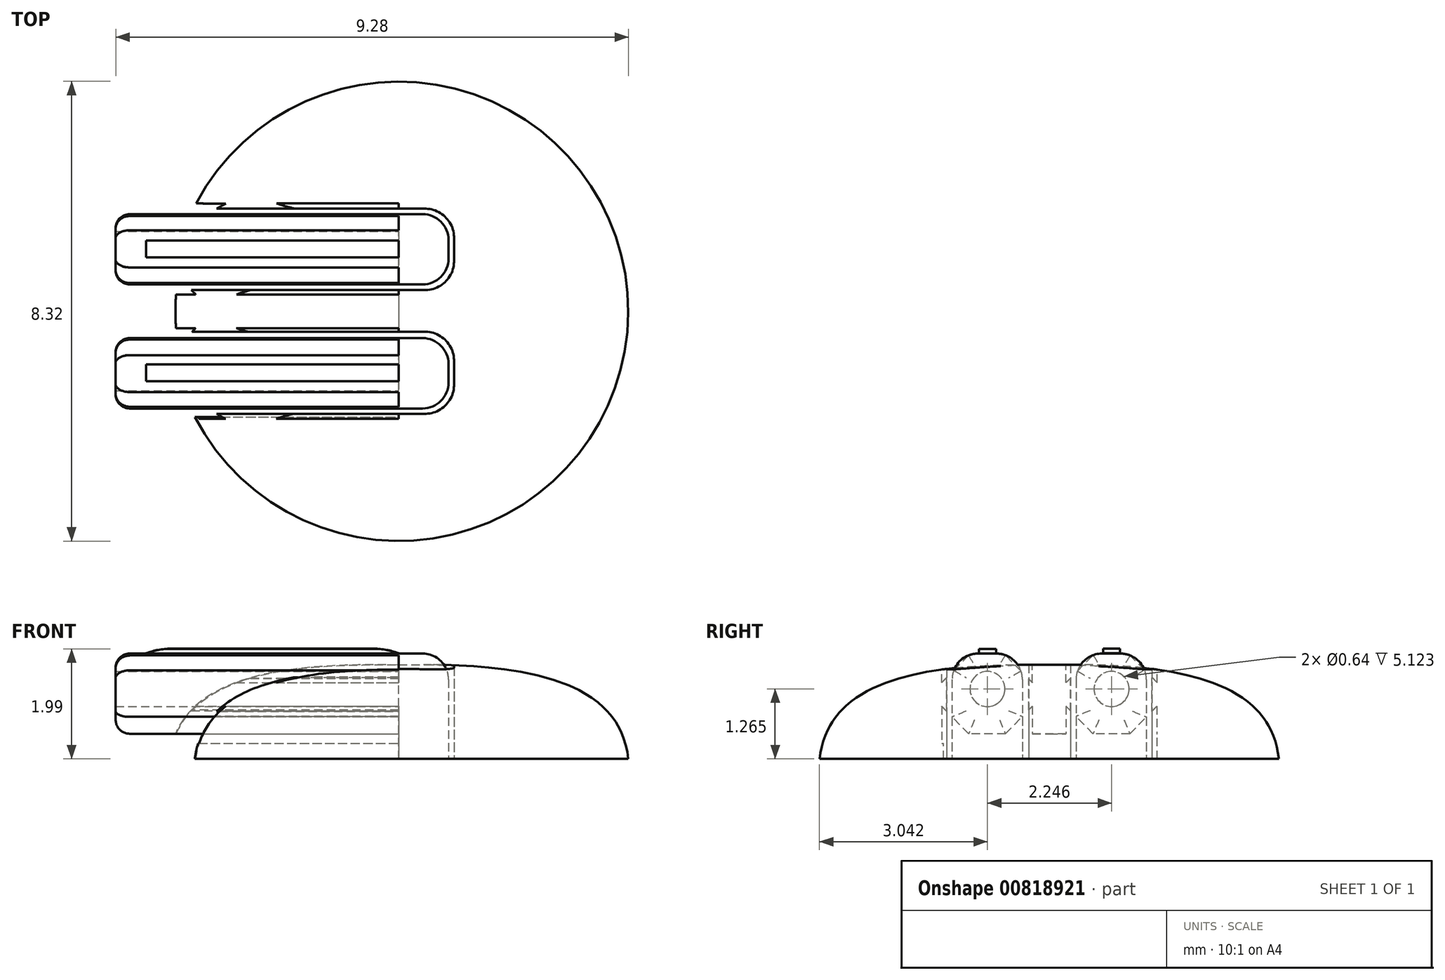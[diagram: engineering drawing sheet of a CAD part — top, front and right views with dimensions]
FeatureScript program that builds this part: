
annotation { "Feature Type Name" : "Feature", "Feature Type Description" : "" }
export const myFeature = defineFeature(function(context is Context, id is Id, definition is map)
    precondition{}
    {
        {
            var Q0;
            Q0=qCreatedBy(makeId("Front.planeOp"),FACE);
            var sketch = newSketch(context, id + "F0", { "sketchPlane" : qUnion([Q0])});
            skFitSpline(sketch, "E0", {"points": [v(0, 1.7) * mm, v(-4.16, 0) * mm], "startDerivative": vector(-6.44, 0.15) * mm, "endDerivative": vector(-0.46, -4.44) * mm});
            skLineSegment(sketch, "E1", {"start": v(-4.16, 0) * mm, "end": v(0, 0) * mm});
            skLineSegment(sketch, "E2", {"start": v(0, 0) * mm, "end": v(0, 1.7) * mm});
            skSolve(sketch);
        }
        {
            var Q0;
            Q0 = qSketchRegion(id + "F0", true);
            var Q1;
            Q1=sQuery(id+"F0.wireOp",EDGE,"E2");
            revolve(context, id + "F1", {"surfaceOperationType" : NewSurfaceOperationType.NEW, "entities" : qUnion([Q0]), "axis" : qUnion([Q1]), "revolveType" : RevolveType.FULL});
        }
        {
            var Q0;
            Q0=qCreatedBy(makeId("Top.planeOp"),FACE);
            var sketch = newSketch(context, id + "F2", { "sketchPlane" : qUnion([Q0])});
            skLineSegment(sketch, "E3.bottom", {"start": v(-4.22, 0.38) * mm, "end": v(1, 0.38) * mm});
            skLineSegment(sketch, "E3.top", {"start": v(-4.22, 1.86) * mm, "end": v(1, 1.86) * mm});
            skLineSegment(sketch, "E3.left", {"start": v(-4.22, 0.38) * mm, "end": v(-4.22, 1.86) * mm});
            skLineSegment(sketch, "E3.right", {"start": v(1, 0.38) * mm, "end": v(1, 1.86) * mm});
            skLineSegment(sketch, "E4.bottom", {"start": v(-4.22, -1.85) * mm, "end": v(1, -1.85) * mm});
            skLineSegment(sketch, "E4.top", {"start": v(-4.22, -0.37) * mm, "end": v(1, -0.37) * mm});
            skLineSegment(sketch, "E4.left", {"start": v(-4.22, -1.85) * mm, "end": v(-4.22, -0.37) * mm});
            skLineSegment(sketch, "E4.right", {"start": v(1, -1.85) * mm, "end": v(1, -0.37) * mm});
            skSolve(sketch);
        }
        {
            var Q0;
            Q0 = qSketchRegion(id + "F2", true);
            extrude(context, id + "F3", {"entities" : qUnion([Q0]), "operationType" : NewBodyOperationType.REMOVE, "depth" : 1.78 * mm, "offsetDistance" : 25.4 * mm});
        }
        {
            var Q0;
            Q0=qCreatedBy(makeId("Top.planeOp"),FACE);
            var sketch = newSketch(context, id + "F4", { "sketchPlane" : qUnion([Q0])});
            skLineSegment(sketch, "E5.bottom", {"start": v(-5.12, -1.76) * mm, "end": v(0.9, -1.76) * mm});
            skLineSegment(sketch, "E5.top", {"start": v(-5.12, -0.49) * mm, "end": v(0.9, -0.49) * mm});
            skLineSegment(sketch, "E5.left", {"start": v(-5.12, -1.76) * mm, "end": v(-5.12, -0.49) * mm});
            skLineSegment(sketch, "E5.right", {"start": v(0.9, -1.76) * mm, "end": v(0.9, -0.49) * mm});
            skLineSegment(sketch, "E6.bottom", {"start": v(-5.12, 0.48) * mm, "end": v(0.9, 0.48) * mm});
            skLineSegment(sketch, "E6.top", {"start": v(-5.12, 1.76) * mm, "end": v(0.9, 1.76) * mm});
            skLineSegment(sketch, "E6.left", {"start": v(-5.12, 0.48) * mm, "end": v(-5.12, 1.76) * mm});
            skLineSegment(sketch, "E6.right", {"start": v(0.9, 0.48) * mm, "end": v(0.9, 1.76) * mm});
            skSolve(sketch);
        }
        {
            var Q0;
            Q0 = qSketchRegion(id + "F4", true);
            extrude(context, id + "F5", {"entities" : qUnion([Q0]), "depth" : 1.9 * mm, "offsetDistance" : 25.4 * mm});
        }
        {
            var Q0;
            Q0=qCreatedBy(makeId("Right.planeOp"),FACE);
            var sketch = newSketch(context, id + "F6", { "sketchPlane" : qUnion([Q0])});
            skLineSegment(sketch, "E7.bottom", {"start": v(1.95, 0) * mm, "end": v(-1.91, 0) * mm});
            skLineSegment(sketch, "E7.top", {"start": v(1.95, 0.45) * mm, "end": v(-1.91, 0.45) * mm});
            skLineSegment(sketch, "E7.left", {"start": v(1.95, 0) * mm, "end": v(1.95, 0.45) * mm});
            skLineSegment(sketch, "E7.right", {"start": v(-1.91, 0) * mm, "end": v(-1.91, 0.45) * mm});
            skLineSegment(sketch, "E8", {"start": v(1.95, 2.05) * mm, "end": v(1.28, 2.05) * mm});
            skLineSegment(sketch, "E9", {"start": v(1.28, 2.05) * mm, "end": v(1.95, 1.38) * mm});
            skLineSegment(sketch, "E10", {"start": v(1.95, 1.38) * mm, "end": v(1.95, 2.05) * mm});
            skLineSegment(sketch, "E11", {"start": v(-0.3, 2.05) * mm, "end": v(-0.97, 2.05) * mm});
            skLineSegment(sketch, "E12", {"start": v(-0.97, 2.05) * mm, "end": v(-0.3, 1.38) * mm});
            skLineSegment(sketch, "E13", {"start": v(-0.3, 1.38) * mm, "end": v(-0.3, 2.05) * mm});
            skLineSegment(sketch, "E14.MirrorCS", {"start": v(-1.95, 2.05) * mm, "end": v(-1.28, 2.05) * mm});
            skLineSegment(sketch, "E15.MirrorCS", {"start": v(-1.95, 1.38) * mm, "end": v(-1.95, 2.05) * mm});
            skLineSegment(sketch, "E16.MirrorCS", {"start": v(0.3, 2.05) * mm, "end": v(0.97, 2.05) * mm});
            skLineSegment(sketch, "E17.MirrorCS", {"start": v(0.97, 2.05) * mm, "end": v(0.3, 1.38) * mm});
            skLineSegment(sketch, "E18.MirrorCS", {"start": v(-1.28, 2.05) * mm, "end": v(-1.95, 1.38) * mm});
            skLineSegment(sketch, "E19.MirrorCS", {"start": v(0.3, 1.38) * mm, "end": v(0.3, 2.05) * mm});
            skLineSegment(sketch, "E20.MirrorCS", {"start": v(0.97, 0.28) * mm, "end": v(0.3, 0.95) * mm});
            skLineSegment(sketch, "E21.MirrorCS", {"start": v(-1.28, 0.28) * mm, "end": v(-1.95, 0.95) * mm});
            skLineSegment(sketch, "E22.MirrorCS", {"start": v(0.3, 0.95) * mm, "end": v(0.3, 0.28) * mm});
            skLineSegment(sketch, "E23.MirrorCS", {"start": v(1.95, 0.95) * mm, "end": v(1.95, 0.28) * mm});
            skLineSegment(sketch, "E24.MirrorCS", {"start": v(0.3, 0.28) * mm, "end": v(0.97, 0.28) * mm});
            skLineSegment(sketch, "E25.MirrorCS", {"start": v(-0.3, 0.28) * mm, "end": v(-0.97, 0.28) * mm});
            skLineSegment(sketch, "E26.MirrorCS", {"start": v(1.28, 0.28) * mm, "end": v(1.95, 0.95) * mm});
            skLineSegment(sketch, "E27.MirrorCS", {"start": v(-0.97, 0.28) * mm, "end": v(-0.3, 0.95) * mm});
            skLineSegment(sketch, "E28.MirrorCS", {"start": v(-0.3, 0.95) * mm, "end": v(-0.3, 0.28) * mm});
            skLineSegment(sketch, "E29.MirrorCS", {"start": v(-1.95, 0.28) * mm, "end": v(-1.28, 0.28) * mm});
            skLineSegment(sketch, "E30.MirrorCS", {"start": v(1.95, 0.28) * mm, "end": v(1.28, 0.28) * mm});
            skLineSegment(sketch, "E31.MirrorCS", {"start": v(-1.95, 0.95) * mm, "end": v(-1.95, 0.28) * mm});
            skSolve(sketch);
        }
        {
            var Q0;
            Q0 = qSketchRegion(id + "F6", true);
            extrude(context, id + "F7", {"entities" : qUnion([Q0]), "operationType" : NewBodyOperationType.REMOVE, "oppositeDirection" : true, "depth" : 5.7 * mm, "offsetDistance" : 25.4 * mm});
        }
        {
            var Q0;
            Q0=makeQuery(id+"F5.opExtrude","CAP_EDGE",EDGE,{"disambiguationData":[OSD([sQuery(id+"F4.wireOp",EDGE,"E6.right")])],"isStart":false});
            var Q1;
            Q1=makeQuery(id+"F5.opExtrude","CAP_EDGE",EDGE,{"disambiguationData":[OSD([sQuery(id+"F4.wireOp",EDGE,"E6.bottom")])],"isStart":false});
            var Q2;
            Q2=makeQuery(id+"F5.opExtrude","CAP_EDGE",EDGE,{"disambiguationData":[OSD([sQuery(id+"F4.wireOp",EDGE,"E6.top")])],"isStart":false});
            var Q3;
            Q3=makeQuery(id+"F5.opExtrude","CAP_EDGE",EDGE,{"disambiguationData":[OSD([sQuery(id+"F4.wireOp",EDGE,"E5.bottom")])],"isStart":false});
            var Q4;
            Q4=makeQuery(id+"F5.opExtrude","CAP_EDGE",EDGE,{"disambiguationData":[OSD([sQuery(id+"F4.wireOp",EDGE,"E5.right")])],"isStart":false});
            var Q5;
            Q5=makeQuery(id+"F5.opExtrude","CAP_EDGE",EDGE,{"disambiguationData":[OSD([sQuery(id+"F4.wireOp",EDGE,"E5.top")])],"isStart":false});
            var Q6;
            Q6=makeQuery(id+"F5.opExtrude","SWEPT_EDGE",EDGE,{"disambiguationData":[OSD([sQuery(id+"F4.wireOp",EDGE,"E6.top"),sQuery(id+"F4.wireOp",EDGE,"E6.right")])]});
            var Q7;
            Q7=makeQuery(id+"F5.opExtrude","SWEPT_EDGE",EDGE,{"disambiguationData":[OSD([sQuery(id+"F4.wireOp",EDGE,"E6.bottom"),sQuery(id+"F4.wireOp",EDGE,"E6.right")])]});
            var Q8;
            Q8=makeQuery(id+"F5.opExtrude","SWEPT_EDGE",EDGE,{"disambiguationData":[OSD([sQuery(id+"F4.wireOp",EDGE,"E5.top"),sQuery(id+"F4.wireOp",EDGE,"E5.right")])]});
            var Q9;
            Q9=makeQuery(id+"F5.opExtrude","SWEPT_EDGE",EDGE,{"disambiguationData":[OSD([sQuery(id+"F4.wireOp",EDGE,"E5.bottom"),sQuery(id+"F4.wireOp",EDGE,"E5.right")])]});
            fillet(context, id + "F8", {"entities" : qUnion([Q0, Q1, Q2, Q3, Q4, Q5, Q6, Q7, Q8, Q9]), "radius" : 0.47 * mm, "tangentPropagation" : true, "allowEdgeOverflow" : false});
        }
        {
            var Q0;
            Q0=qCreatedBy(makeId("Right.planeOp"),FACE);
            var sketch = newSketch(context, id + "F9", { "sketchPlane" : qUnion([Q0])});
            skLineSegment(sketch, "E32.bottom", {"start": v(1.28, 2) * mm, "end": v(0.97, 2) * mm});
            skLineSegment(sketch, "E32.top", {"start": v(1.28, 1.91) * mm, "end": v(0.97, 1.91) * mm});
            skLineSegment(sketch, "E32.left", {"start": v(1.28, 2) * mm, "end": v(1.28, 1.91) * mm});
            skLineSegment(sketch, "E32.right", {"start": v(0.97, 2) * mm, "end": v(0.97, 1.91) * mm});
            skLineSegment(sketch, "E33.bottom", {"start": v(-0.96, 2) * mm, "end": v(-1.27, 2) * mm});
            skLineSegment(sketch, "E33.top", {"start": v(-0.96, 1.9) * mm, "end": v(-1.27, 1.9) * mm});
            skLineSegment(sketch, "E33.left", {"start": v(-0.96, 2) * mm, "end": v(-0.96, 1.9) * mm});
            skLineSegment(sketch, "E33.right", {"start": v(-1.27, 2) * mm, "end": v(-1.27, 1.9) * mm});
            skSolve(sketch);
        }
        {
            var Q0;
            Q0 = qSketchRegion(id + "F9", true);
            extrude(context, id + "F10", {"entities" : qUnion([Q0]), "oppositeDirection" : true, "depth" : 4.57 * mm, "offsetDistance" : 25.4 * mm});
        }
        {
            var Q0;
            Q0=qCreatedBy(makeId("Right.planeOp"),FACE);
            var sketch = newSketch(context, id + "F11", { "sketchPlane" : qUnion([Q0])});
            skCircle(sketch, "E34", {"center": v(1.13, 1.26) * mm, "radius": 0.32 * mm});
            skCircle(sketch, "E35", {"center": v(-1.12, 1.26) * mm, "radius": 0.32 * mm});
            skSolve(sketch);
        }
        {
            var Q0;
            Q0 = qSketchRegion(id + "F11", true);
            extrude(context, id + "F12", {"entities" : qUnion([Q0]), "operationType" : NewBodyOperationType.REMOVE, "oppositeDirection" : true, "depth" : 5.94 * mm, "offsetDistance" : 25.4 * mm});
        }
        {
            var Q0;
            Q0=makeQuery(id+"F3.boolean.opBoolean","COPY",EDGE,{"derivedFrom":makeQuery(id+"F3.opExtrude","SWEPT_EDGE",EDGE,{"disambiguationData":[OSD([sQuery(id+"F2.wireOp",EDGE,"E3.top"),sQuery(id+"F2.wireOp",EDGE,"E3.right")])]})});
            var Q1;
            Q1=makeQuery(id+"F3.boolean.opBoolean","COPY",EDGE,{"derivedFrom":makeQuery(id+"F3.opExtrude","SWEPT_EDGE",EDGE,{"disambiguationData":[OSD([sQuery(id+"F2.wireOp",EDGE,"E3.bottom"),sQuery(id+"F2.wireOp",EDGE,"E3.right")])]})});
            var Q2;
            Q2=makeQuery(id+"F3.boolean.opBoolean","COPY",EDGE,{"derivedFrom":makeQuery(id+"F3.opExtrude","SWEPT_EDGE",EDGE,{"disambiguationData":[OSD([sQuery(id+"F2.wireOp",EDGE,"E4.bottom"),sQuery(id+"F2.wireOp",EDGE,"E4.right")])]})});
            var Q3;
            Q3=makeQuery(id+"F3.boolean.opBoolean","COPY",EDGE,{"derivedFrom":makeQuery(id+"F3.opExtrude","SWEPT_EDGE",EDGE,{"disambiguationData":[OSD([sQuery(id+"F2.wireOp",EDGE,"E4.top"),sQuery(id+"F2.wireOp",EDGE,"E4.right")])]})});
            fillet(context, id + "F13", {"entities" : qUnion([Q0, Q1, Q2, Q3]), "radius" : 0.5 * mm, "tangentPropagation" : true, "allowEdgeOverflow" : false});
        }
        {
            var Q0;
            Q0=makeQuery(id+"F7.boolean.opBoolean","INTERSECT",EDGE,{"derivedFrom":[makeQuery(id+"F5.opExtrude","SWEPT_FACE",FACE,{"disambiguationData":[OSD([sQuery(id+"F4.wireOp",EDGE,"E6.left")])]}),makeQuery(id+"F7.opExtrude","SWEPT_FACE",FACE,{"disambiguationData":[OSD([sQuery(id+"F6.wireOp",EDGE,"E17.MirrorCS")])]})]});
            var Q1;
            Q1=makeQuery(id+"F5.opExtrude","SWEPT_EDGE",EDGE,{"disambiguationData":[OSD([sQuery(id+"F4.wireOp",EDGE,"E6.bottom"),sQuery(id+"F4.wireOp",EDGE,"E6.left")])]});
            var Q2;
            Q2=makeQuery(id+"F7.boolean.opBoolean","INTERSECT",EDGE,{"derivedFrom":[makeQuery(id+"F5.opExtrude","SWEPT_FACE",FACE,{"disambiguationData":[OSD([sQuery(id+"F4.wireOp",EDGE,"E6.left")])]}),makeQuery(id+"F7.opExtrude","SWEPT_FACE",FACE,{"disambiguationData":[OSD([sQuery(id+"F6.wireOp",EDGE,"E20.MirrorCS")])]})]});
            var Q3;
            {var subQ0=sQuery(id+"F6.wireOp",EDGE,"E7.top");Q3=makeQuery(id+"F7.boolean.opBoolean","INTERSECT",EDGE,{"derivedFrom":[makeQuery(id+"F5.opExtrude","SWEPT_FACE",FACE,{"disambiguationData":[OSD([sQuery(id+"F4.wireOp",EDGE,"E6.left")])]}),makeQuery(id+"F7.opExtrude","SWEPT_FACE",FACE,{"disambiguationData":[OSD([subQ0]),TDD([makeQuery(id+"F6.imprint","IMPRINT",EDGE,{"disambiguationData":[TD([[makeQuery(id+"F6.imprint","INTERSECT",VERTEX,{"derivedFrom":[subQ0,sQuery(id+"F6.wireOp",EDGE,"E26.MirrorCS")]}),-1.0]])],"derivedFrom":subQ0})])]})]});}
            var Q4;
            Q4=makeQuery(id+"F7.boolean.opBoolean","INTERSECT",EDGE,{"derivedFrom":[makeQuery(id+"F5.opExtrude","SWEPT_FACE",FACE,{"disambiguationData":[OSD([sQuery(id+"F4.wireOp",EDGE,"E6.left")])]}),makeQuery(id+"F7.opExtrude","SWEPT_FACE",FACE,{"disambiguationData":[OSD([sQuery(id+"F6.wireOp",EDGE,"E26.MirrorCS")])]})]});
            var Q5;
            Q5=makeQuery(id+"F5.opExtrude","SWEPT_EDGE",EDGE,{"disambiguationData":[OSD([sQuery(id+"F4.wireOp",EDGE,"E6.top"),sQuery(id+"F4.wireOp",EDGE,"E6.left")])]});
            var Q6;
            Q6=makeQuery(id+"F7.boolean.opBoolean","INTERSECT",EDGE,{"derivedFrom":[makeQuery(id+"F5.opExtrude","SWEPT_FACE",FACE,{"disambiguationData":[OSD([sQuery(id+"F4.wireOp",EDGE,"E6.left")])]}),makeQuery(id+"F7.opExtrude","SWEPT_FACE",FACE,{"disambiguationData":[OSD([sQuery(id+"F6.wireOp",EDGE,"E9")])]})]});
            var Q7;
            Q7=makeQuery(id+"F5.opExtrude","CAP_EDGE",EDGE,{"disambiguationData":[OSD([sQuery(id+"F4.wireOp",EDGE,"E6.left")])],"isStart":false});
            var Q8;
            Q8=makeQuery(id+"F7.boolean.opBoolean","INTERSECT",EDGE,{"derivedFrom":[makeQuery(id+"F5.opExtrude","SWEPT_FACE",FACE,{"disambiguationData":[OSD([sQuery(id+"F4.wireOp",EDGE,"E5.left")])]}),makeQuery(id+"F7.opExtrude","SWEPT_FACE",FACE,{"disambiguationData":[OSD([sQuery(id+"F6.wireOp",EDGE,"E12")])]})]});
            var Q9;
            Q9=makeQuery(id+"F5.opExtrude","SWEPT_EDGE",EDGE,{"disambiguationData":[OSD([sQuery(id+"F4.wireOp",EDGE,"E5.top"),sQuery(id+"F4.wireOp",EDGE,"E5.left")])]});
            var Q10;
            Q10=makeQuery(id+"F7.boolean.opBoolean","INTERSECT",EDGE,{"derivedFrom":[makeQuery(id+"F5.opExtrude","SWEPT_FACE",FACE,{"disambiguationData":[OSD([sQuery(id+"F4.wireOp",EDGE,"E5.left")])]}),makeQuery(id+"F7.opExtrude","SWEPT_FACE",FACE,{"disambiguationData":[OSD([sQuery(id+"F6.wireOp",EDGE,"E27.MirrorCS")])]})]});
            var Q11;
            {var subQ0=sQuery(id+"F6.wireOp",EDGE,"E7.top");Q11=makeQuery(id+"F7.boolean.opBoolean","INTERSECT",EDGE,{"derivedFrom":[makeQuery(id+"F5.opExtrude","SWEPT_FACE",FACE,{"disambiguationData":[OSD([sQuery(id+"F4.wireOp",EDGE,"E5.left")])]}),makeQuery(id+"F7.opExtrude","SWEPT_FACE",FACE,{"disambiguationData":[OSD([subQ0]),TDD([makeQuery(id+"F6.imprint","IMPRINT",EDGE,{"disambiguationData":[TD([[makeQuery(id+"F6.imprint","INTERSECT",VERTEX,{"derivedFrom":[subQ0,sQuery(id+"F6.wireOp",EDGE,"E27.MirrorCS")]}),-1.0]])],"derivedFrom":subQ0})])]})]});}
            var Q12;
            Q12=makeQuery(id+"F7.boolean.opBoolean","INTERSECT",EDGE,{"derivedFrom":[makeQuery(id+"F5.opExtrude","SWEPT_FACE",FACE,{"disambiguationData":[OSD([sQuery(id+"F4.wireOp",EDGE,"E5.left")])]}),makeQuery(id+"F7.opExtrude","SWEPT_FACE",FACE,{"disambiguationData":[OSD([sQuery(id+"F6.wireOp",EDGE,"E21.MirrorCS")])]})]});
            var Q13;
            Q13=makeQuery(id+"F5.opExtrude","SWEPT_EDGE",EDGE,{"disambiguationData":[OSD([sQuery(id+"F4.wireOp",EDGE,"E5.bottom"),sQuery(id+"F4.wireOp",EDGE,"E5.left")])]});
            var Q14;
            Q14=makeQuery(id+"F7.boolean.opBoolean","INTERSECT",EDGE,{"derivedFrom":[makeQuery(id+"F5.opExtrude","SWEPT_FACE",FACE,{"disambiguationData":[OSD([sQuery(id+"F4.wireOp",EDGE,"E5.left")])]}),makeQuery(id+"F7.opExtrude","SWEPT_FACE",FACE,{"disambiguationData":[OSD([sQuery(id+"F6.wireOp",EDGE,"E18.MirrorCS")])]})]});
            var Q15;
            Q15=makeQuery(id+"F8.opFillet","BLEND_EDGE",EDGE,{"disambiguationData":[OD(0.0)],"blendedFrom":[makeQuery(id+"F5.opExtrude","CAP_EDGE",EDGE,{"disambiguationData":[OSD([sQuery(id+"F4.wireOp",EDGE,"E5.bottom")])],"isStart":false}),makeQuery(id+"F5.opExtrude","SWEPT_FACE",FACE,{"disambiguationData":[OSD([sQuery(id+"F4.wireOp",EDGE,"E5.left")])]})],"blendedInto":[makeQuery(id+"F5.opExtrude","SWEPT_FACE",FACE,{"disambiguationData":[OSD([sQuery(id+"F4.wireOp",EDGE,"E5.left")])]})]});
            var Q16;
            Q16=makeQuery(id+"F8.opFillet","BLEND_EDGE",EDGE,{"disambiguationData":[OD(1.0)],"blendedFrom":[makeQuery(id+"F5.opExtrude","CAP_EDGE",EDGE,{"disambiguationData":[OSD([sQuery(id+"F4.wireOp",EDGE,"E5.top")])],"isStart":false}),makeQuery(id+"F5.opExtrude","SWEPT_FACE",FACE,{"disambiguationData":[OSD([sQuery(id+"F4.wireOp",EDGE,"E5.left")])]})],"blendedInto":[makeQuery(id+"F5.opExtrude","SWEPT_FACE",FACE,{"disambiguationData":[OSD([sQuery(id+"F4.wireOp",EDGE,"E5.left")])]})]});
            var Q17;
            Q17=makeQuery(id+"F8.opFillet","BLEND_EDGE",EDGE,{"disambiguationData":[OD(0.0)],"blendedFrom":[makeQuery(id+"F5.opExtrude","CAP_EDGE",EDGE,{"disambiguationData":[OSD([sQuery(id+"F4.wireOp",EDGE,"E5.top")])],"isStart":false}),makeQuery(id+"F5.opExtrude","SWEPT_FACE",FACE,{"disambiguationData":[OSD([sQuery(id+"F4.wireOp",EDGE,"E5.left")])]})],"blendedInto":[makeQuery(id+"F5.opExtrude","SWEPT_FACE",FACE,{"disambiguationData":[OSD([sQuery(id+"F4.wireOp",EDGE,"E5.left")])]})]});
            var Q18;
            Q18=makeQuery(id+"F5.opExtrude","CAP_EDGE",EDGE,{"disambiguationData":[OSD([sQuery(id+"F4.wireOp",EDGE,"E5.left")])],"isStart":false});
            var Q19;
            Q19=makeQuery(id+"F8.opFillet","BLEND_EDGE",EDGE,{"disambiguationData":[OD(1.0)],"blendedFrom":[makeQuery(id+"F5.opExtrude","CAP_EDGE",EDGE,{"disambiguationData":[OSD([sQuery(id+"F4.wireOp",EDGE,"E5.bottom")])],"isStart":false}),makeQuery(id+"F5.opExtrude","SWEPT_FACE",FACE,{"disambiguationData":[OSD([sQuery(id+"F4.wireOp",EDGE,"E5.left")])]})],"blendedInto":[makeQuery(id+"F5.opExtrude","SWEPT_FACE",FACE,{"disambiguationData":[OSD([sQuery(id+"F4.wireOp",EDGE,"E5.left")])]})]});
            var Q20;
            Q20=makeQuery(id+"F8.opFillet","BLEND_EDGE",EDGE,{"disambiguationData":[OD(1.0)],"blendedFrom":[makeQuery(id+"F5.opExtrude","CAP_EDGE",EDGE,{"disambiguationData":[OSD([sQuery(id+"F4.wireOp",EDGE,"E6.bottom")])],"isStart":false}),makeQuery(id+"F5.opExtrude","SWEPT_FACE",FACE,{"disambiguationData":[OSD([sQuery(id+"F4.wireOp",EDGE,"E6.left")])]})],"blendedInto":[makeQuery(id+"F5.opExtrude","SWEPT_FACE",FACE,{"disambiguationData":[OSD([sQuery(id+"F4.wireOp",EDGE,"E6.left")])]})]});
            var Q21;
            Q21=makeQuery(id+"F8.opFillet","BLEND_EDGE",EDGE,{"disambiguationData":[OD(0.0)],"blendedFrom":[makeQuery(id+"F5.opExtrude","CAP_EDGE",EDGE,{"disambiguationData":[OSD([sQuery(id+"F4.wireOp",EDGE,"E6.top")])],"isStart":false}),makeQuery(id+"F5.opExtrude","SWEPT_FACE",FACE,{"disambiguationData":[OSD([sQuery(id+"F4.wireOp",EDGE,"E6.left")])]})],"blendedInto":[makeQuery(id+"F5.opExtrude","SWEPT_FACE",FACE,{"disambiguationData":[OSD([sQuery(id+"F4.wireOp",EDGE,"E6.left")])]})]});
            var Q22;
            Q22=makeQuery(id+"F8.opFillet","BLEND_EDGE",EDGE,{"disambiguationData":[OD(1.0)],"blendedFrom":[makeQuery(id+"F5.opExtrude","CAP_EDGE",EDGE,{"disambiguationData":[OSD([sQuery(id+"F4.wireOp",EDGE,"E6.top")])],"isStart":false}),makeQuery(id+"F5.opExtrude","SWEPT_FACE",FACE,{"disambiguationData":[OSD([sQuery(id+"F4.wireOp",EDGE,"E6.left")])]})],"blendedInto":[makeQuery(id+"F5.opExtrude","SWEPT_FACE",FACE,{"disambiguationData":[OSD([sQuery(id+"F4.wireOp",EDGE,"E6.left")])]})]});
            var Q23;
            Q23=makeQuery(id+"F8.opFillet","BLEND_EDGE",EDGE,{"disambiguationData":[OD(0.0)],"blendedFrom":[makeQuery(id+"F5.opExtrude","CAP_EDGE",EDGE,{"disambiguationData":[OSD([sQuery(id+"F4.wireOp",EDGE,"E6.bottom")])],"isStart":false}),makeQuery(id+"F5.opExtrude","SWEPT_FACE",FACE,{"disambiguationData":[OSD([sQuery(id+"F4.wireOp",EDGE,"E6.left")])]})],"blendedInto":[makeQuery(id+"F5.opExtrude","SWEPT_FACE",FACE,{"disambiguationData":[OSD([sQuery(id+"F4.wireOp",EDGE,"E6.left")])]})]});
            fillet(context, id + "F14", {"entities" : qUnion([Q0, Q1, Q2, Q3, Q4, Q5, Q6, Q7, Q8, Q9, Q10, Q11, Q12, Q13, Q14, Q15, Q16, Q17, Q18, Q19, Q20, Q21, Q22, Q23]), "radius" : 0.25 * mm, "tangentPropagation" : true, "allowEdgeOverflow" : false});
        }
        {
            var Q0;
            Q0=makeQuery(id+"F10.opExtrude","CAP_EDGE",EDGE,{"disambiguationData":[OSD([sQuery(id+"F9.wireOp",EDGE,"E33.bottom")])],"isStart":false});
            var Q1;
            Q1=makeQuery(id+"F10.opExtrude","CAP_EDGE",EDGE,{"disambiguationData":[OSD([sQuery(id+"F9.wireOp",EDGE,"E32.bottom")])],"isStart":false});
            var Q2;
            Q2=makeQuery(id+"F10.opExtrude","CAP_EDGE",EDGE,{"disambiguationData":[OSD([sQuery(id+"F9.wireOp",EDGE,"E32.bottom")])],"isStart":true});
            var Q3;
            Q3=makeQuery(id+"F10.opExtrude","CAP_EDGE",EDGE,{"disambiguationData":[OSD([sQuery(id+"F9.wireOp",EDGE,"E33.bottom")])],"isStart":true});
            fillet(context, id + "F15", {"entities" : qUnion([Q0, Q1, Q2, Q3]), "radius" : 1.27 * mm, "tangentPropagation" : true, "allowEdgeOverflow" : false});
        }
    });
